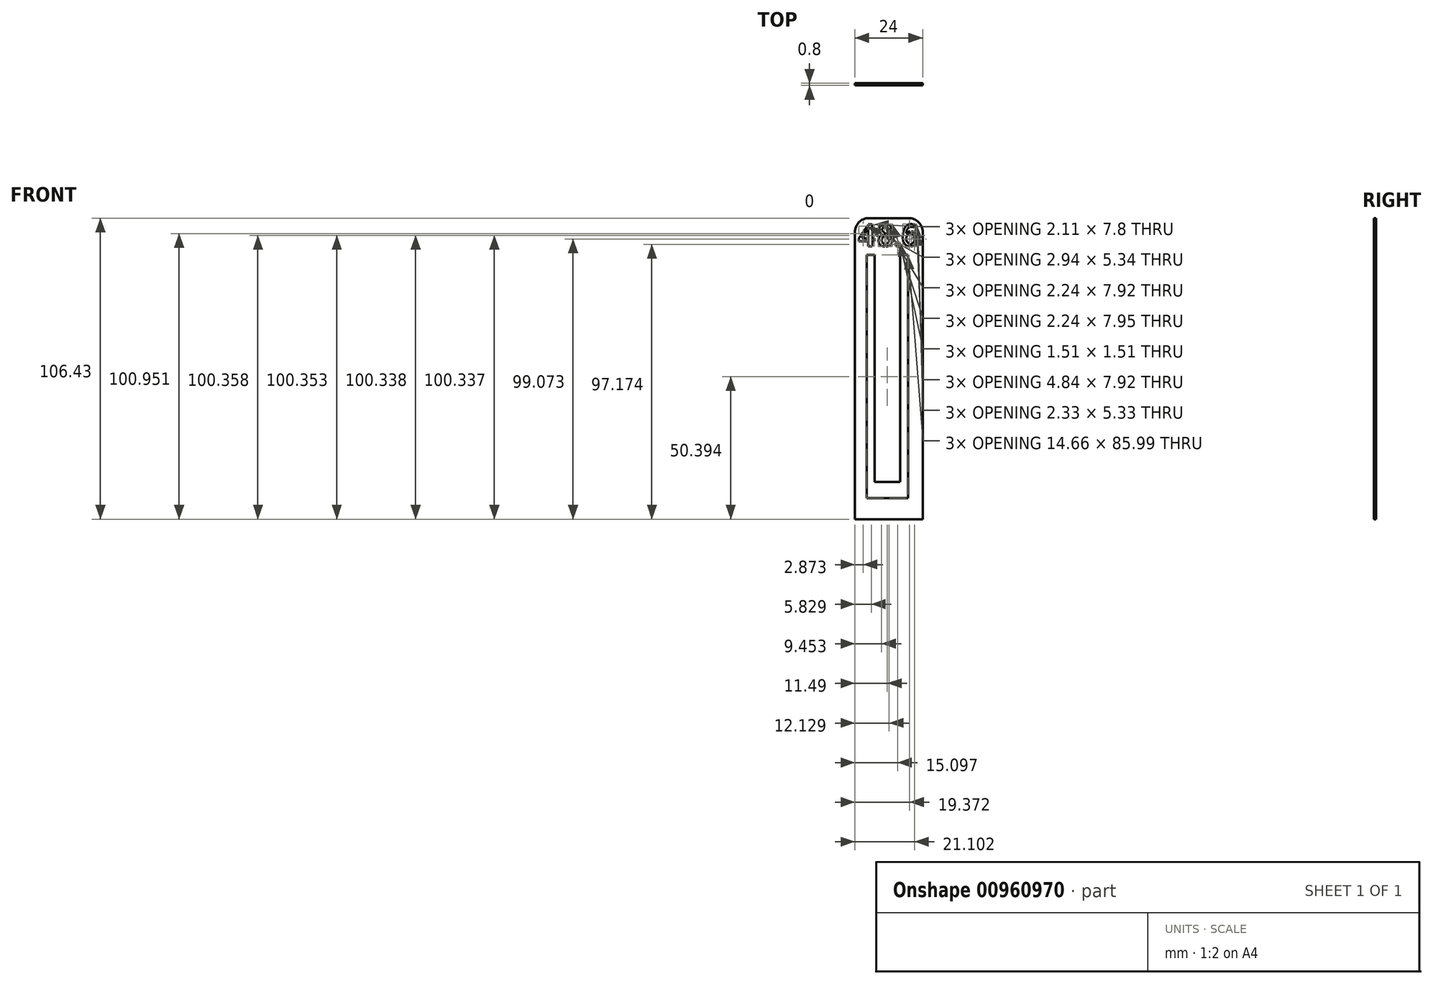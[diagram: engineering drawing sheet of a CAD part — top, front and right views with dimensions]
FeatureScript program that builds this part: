
annotation { "Feature Type Name" : "Feature", "Feature Type Description" : "" }
export const myFeature = defineFeature(function(context is Context, id is Id, definition is map)
    precondition{}
    {
        {
            var Q0;
            Q0=qCreatedBy(makeId("Front.planeOp"),FACE);
            var sketch = newSketch(context, id + "F0", { "sketchPlane" : qUnion([Q0])});
            skLineSegment(sketch, "E0.bottom", {"start": v(-11.49, 13.04) * mm, "end": v(12.51, 13.04) * mm});
            skLineSegment(sketch, "E0.top", {"start": v(-11.49, -93.39) * mm, "end": v(12.51, -93.39) * mm});
            skLineSegment(sketch, "E0.left", {"start": v(-11.49, 13.04) * mm, "end": v(-11.49, -93.39) * mm});
            skLineSegment(sketch, "E0.right", {"start": v(12.51, 13.04) * mm, "end": v(12.51, -93.39) * mm});
            skLineSegment(sketch, "E1", {"start": v(-7.33, 0) * mm, "end": v(-7.33, -93.39) * mm});
            skLineSegment(sketch, "E2", {"start": v(-7.33, 0) * mm, "end": v(-4.47, 0) * mm});
            skLineSegment(sketch, "E3", {"start": v(-4.47, 0) * mm, "end": v(-4.47, -93.39) * mm});
            skPoint(sketch, "E3.endSnap0", {"position": v(0.51, -93.39) * mm});
            skLineSegment(sketch, "E4.MirrorCS", {"start": v(4.47, 0) * mm, "end": v(4.47, -93.39) * mm});
            skLineSegment(sketch, "E5.MirrorCS", {"start": v(7.33, 0) * mm, "end": v(4.47, 0) * mm});
            skLineSegment(sketch, "E6.MirrorCS", {"start": v(7.33, 0) * mm, "end": v(7.33, -93.39) * mm});
            skLineSegment(sketch, "E7", {"start": v(-7.33, -86) * mm, "end": v(7.33, -86) * mm});
            skLineSegment(sketch, "E8", {"start": v(-4.47, -80.21) * mm, "end": v(4.47, -80.21) * mm});
            skText(sketch, "E9", { "text": "48.6", "fontName": "AllertaStencil-Regular.ttf"});
            const initialGuessF0  = {"E9": [-0.01049, 0.00307, 1, 0, 0.0078]};
            skSetInitialGuess(sketch, initialGuessF0);
            skSolve(sketch);
        }
        {
            var Q0;
            {var subQ1=sQuery(id+"F0.wireOp",EDGE,"E0.left");Q0=makeQuery(id+"F0.imprint","IMPRINT",FACE,{"disambiguationData":[TD([[makeQuery(id+"F0.imprint","IMPRINT",EDGE,{"derivedFrom":subQ1}),1.0]])]});}
            var Q1;
            {var subQ0=sQuery(id+"F0.wireOp",EDGE,"E0.bottom");var subQ1=sQuery(id+"F0.wireOp",EDGE,"j7jo4HVO-TDq1-Ujr7-fj7i-QEgA1FUm5snF");var subQ2=makeQuery(id+"F0.imprint","INTERSECT",VERTEX,{"disambiguationData":[OD(0.0)],"derivedFrom":[subQ1,subQ0]});Q1=makeQuery(id+"F0.imprint","IMPRINT",FACE,{"disambiguationData":[TD([[makeQuery(id+"F0.imprint","IMPRINT",EDGE,{"disambiguationData":[TD([[subQ2,1.0]])],"derivedFrom":subQ1}),1.0]])]});}
            var Q2;
            {var subQ0=sQuery(id+"F0.wireOp",EDGE,"E0.bottom");var subQ1=sQuery(id+"F0.wireOp",EDGE,"j7jo4HVO-TDq1-Ujr7-fj7i-QEgA1FUm5snF");var subQ2=makeQuery(id+"F0.imprint","INTERSECT",VERTEX,{"disambiguationData":[OD(0.0)],"derivedFrom":[subQ1,subQ0]});Q2=makeQuery(id+"F0.imprint","IMPRINT",FACE,{"disambiguationData":[TD([[makeQuery(id+"F0.imprint","IMPRINT",EDGE,{"disambiguationData":[TD([[subQ2,-1.0]])],"derivedFrom":subQ1}),1.0]])]});}
            var Q3;
            {var subQ0=sQuery(id+"F0.wireOp",EDGE,"E4.MirrorCS");var subQ1=sQuery(id+"F0.wireOp",EDGE,"E0.top");var subQ2=makeQuery(id+"F0.imprint","INTERSECT",VERTEX,{"derivedFrom":[subQ1,subQ0]});Q3=makeQuery(id+"F0.imprint","IMPRINT",FACE,{"disambiguationData":[TD([[makeQuery(id+"F0.imprint","IMPRINT",EDGE,{"disambiguationData":[TD([[subQ2,-1.0]])],"derivedFrom":subQ1}),1.0]])]});}
            var Q4;
            {var subQ0=sQuery(id+"F0.wireOp",EDGE,"E3");var subQ1=sQuery(id+"F0.wireOp",EDGE,"E0.top");var subQ2=makeQuery(id+"F0.imprint","INTERSECT",VERTEX,{"derivedFrom":[subQ1,subQ0]});Q4=makeQuery(id+"F0.imprint","IMPRINT",FACE,{"disambiguationData":[TD([[makeQuery(id+"F0.imprint","IMPRINT",EDGE,{"disambiguationData":[TD([[subQ2,-1.0]])],"derivedFrom":subQ1}),1.0]])]});}
            var Q5;
            {var subQ0=sQuery(id+"F0.wireOp",EDGE,"E1");var subQ1=sQuery(id+"F0.wireOp",EDGE,"E0.top");var subQ2=makeQuery(id+"F0.imprint","INTERSECT",VERTEX,{"derivedFrom":[subQ1,subQ0]});Q5=makeQuery(id+"F0.imprint","IMPRINT",FACE,{"disambiguationData":[TD([[makeQuery(id+"F0.imprint","IMPRINT",EDGE,{"disambiguationData":[TD([[subQ2,-1.0]])],"derivedFrom":subQ1}),1.0]])]});}
            extrude(context, id + "F1", {"entities" : qUnion([Q0, Q1, Q2, Q3, Q4, Q5]), "depth" : .8 * mm, "offsetDistance" : 25 * mm});
        }
        {
            var Q0;
            Q0=makeQuery(id+"F1.opExtrude","SWEPT_EDGE",EDGE,{"disambiguationData":[OSD([sQuery(id+"F0.wireOp",EDGE,"E0.bottom"),sQuery(id+"F0.wireOp",EDGE,"E0.left")])]});
            var Q1;
            Q1=makeQuery(id+"F1.opExtrude","SWEPT_EDGE",EDGE,{"disambiguationData":[OSD([sQuery(id+"F0.wireOp",EDGE,"E0.bottom"),sQuery(id+"F0.wireOp",EDGE,"E0.right")])]});
            fillet(context, id + "F2", {"entities" : qUnion([Q0, Q1]), "radius" : 5 * mm, "tangentPropagation" : true, "allowEdgeOverflow" : false});
        }
    });
